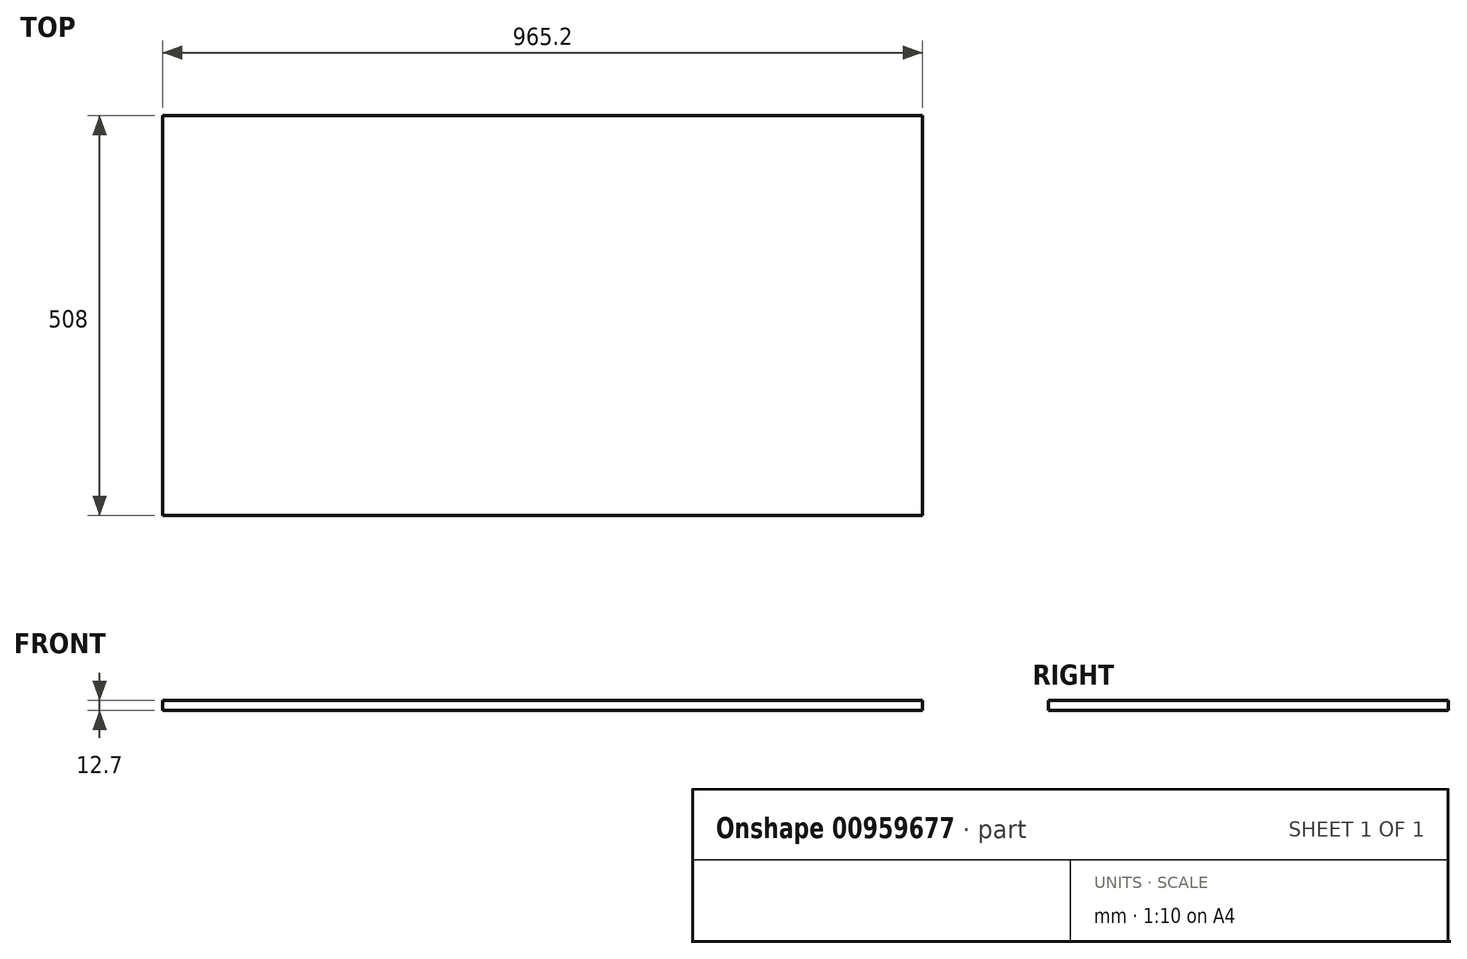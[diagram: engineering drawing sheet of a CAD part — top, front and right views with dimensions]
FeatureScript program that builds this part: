
annotation { "Feature Type Name" : "Feature", "Feature Type Description" : "" }
export const myFeature = defineFeature(function(context is Context, id is Id, definition is map)
    precondition{}
    {
        {
            var Q0;
            Q0=qCreatedBy(makeId("Top.planeOp"),FACE);
            var sketch = newSketch(context, id + "F0", { "sketchPlane" : qUnion([Q0])});
            skLineSegment(sketch, "E0.bottom", {"start": v(-552.95, 314.83) * mm, "end": v(412.25, 314.83) * mm});
            skLineSegment(sketch, "E0.top", {"start": v(-552.95, -193.17) * mm, "end": v(412.25, -193.17) * mm});
            skLineSegment(sketch, "E0.left", {"start": v(-552.95, 314.83) * mm, "end": v(-552.95, -193.17) * mm});
            skLineSegment(sketch, "E0.right", {"start": v(412.25, 314.83) * mm, "end": v(412.25, -193.17) * mm});
            skSolve(sketch);
        }
        {
            var Q0;
            Q0=makeQuery(id+"F0.imprint","IMPRINT",FACE,{"disambiguationData":[TD([[makeQuery(id+"F0.imprint","IMPRINT",EDGE,{"derivedFrom":sQuery(id+"F0.wireOp",EDGE,"E0.bottom")}),-1.0]])]});
            extrude(context, id + "F1", {"entities" : qUnion([Q0]), "depth" : 12.7 * mm, "offsetDistance" : 25.4 * mm});
        }
    });
